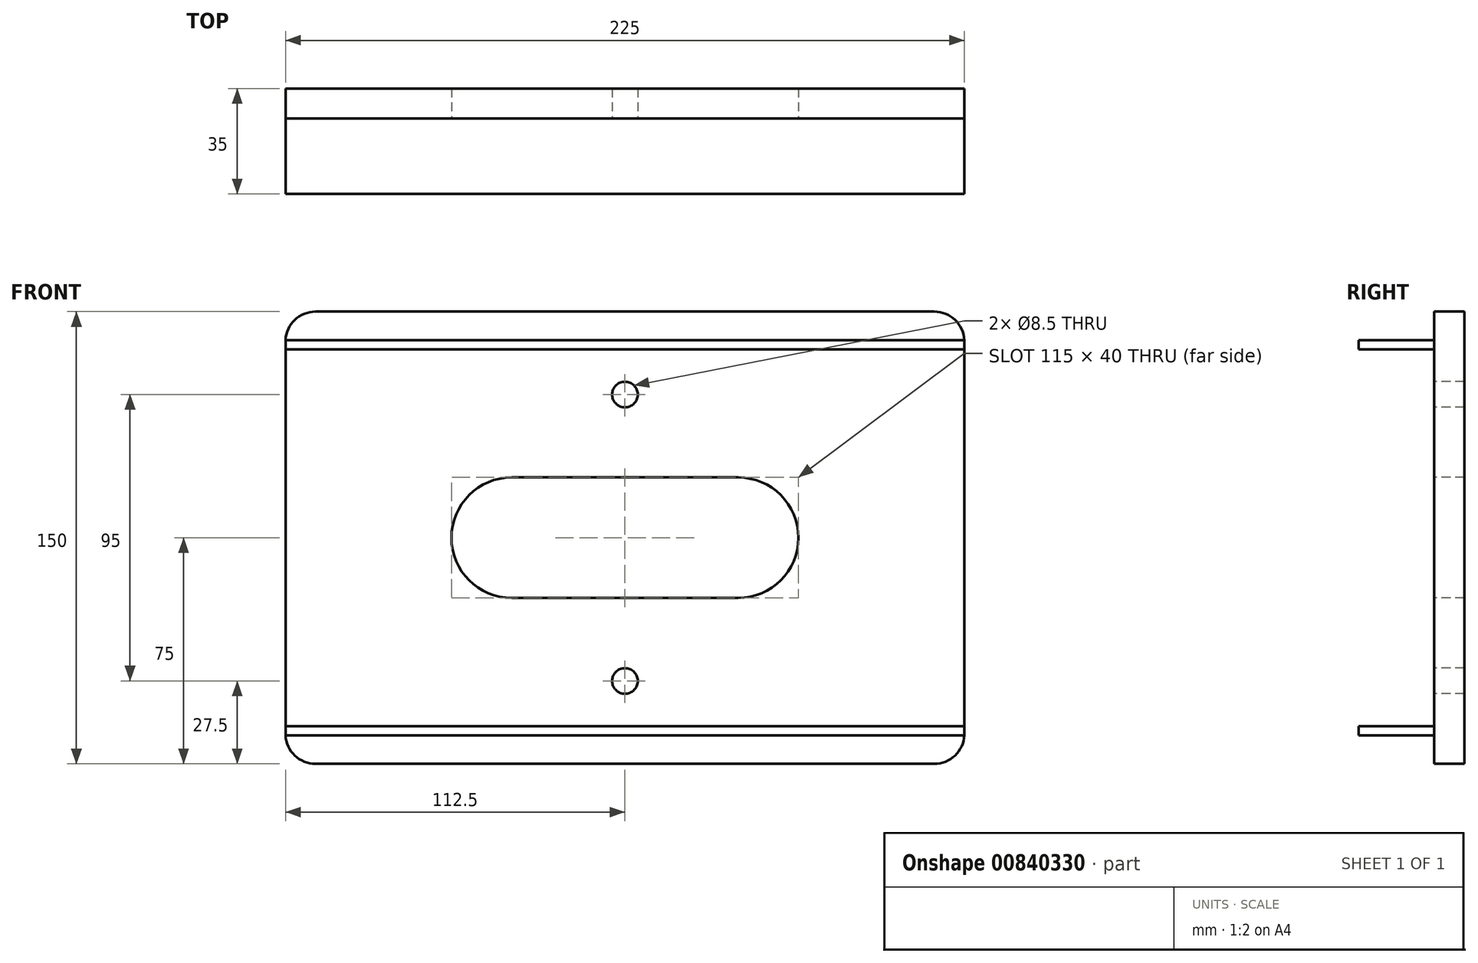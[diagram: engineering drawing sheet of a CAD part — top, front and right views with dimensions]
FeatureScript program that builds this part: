
annotation { "Feature Type Name" : "Feature", "Feature Type Description" : "" }
export const myFeature = defineFeature(function(context is Context, id is Id, definition is map)
    precondition{}
    {
        {
            var Q0;
            Q0=qCreatedBy(makeId("Front.planeOp"),FACE);
            var sketch = newSketch(context, id + "F0", { "sketchPlane" : qUnion([Q0])});
            skLineSegment(sketch, "E0.bottom", {"start": v(-112.5, 75) * mm, "end": v(112.5, 75) * mm});
            skLineSegment(sketch, "E0.top", {"start": v(-112.5, -75) * mm, "end": v(112.5, -75) * mm});
            skLineSegment(sketch, "E0.left", {"start": v(-112.5, 75) * mm, "end": v(-112.5, -75) * mm});
            skLineSegment(sketch, "E0.right", {"start": v(112.5, 75) * mm, "end": v(112.5, -75) * mm});
            skPoint(sketch, "E0.middle", {"position": v(0, 0) * mm});
            skCircle(sketch, "E1", {"center": v(0, 0) * mm, "radius": 20 * mm});
            skSolve(sketch);
        }
        {
            var Q0;
            Q0=qSketchRegion(id+"F0",true);
            extrude(context, id + "F1", {"entities" : qUnion([Q0]), "endBound" : BoundingType.SYMMETRIC, "depth" : 10 * mm, "offsetDistance" : 25 * mm});
        }
        {
            var Q0;
            Q0=makeQuery(id+"F1.opExtrude","SWEPT_EDGE",EDGE,{"disambiguationData":[OSD([sQuery(id+"F0.wireOp",EDGE,"E0.bottom"),sQuery(id+"F0.wireOp",EDGE,"E0.left")])]});
            var Q1;
            Q1=makeQuery(id+"F1.opExtrude","SWEPT_EDGE",EDGE,{"disambiguationData":[OSD([sQuery(id+"F0.wireOp",EDGE,"E0.bottom"),sQuery(id+"F0.wireOp",EDGE,"E0.right")])]});
            var Q2;
            Q2=makeQuery(id+"F1.opExtrude","SWEPT_EDGE",EDGE,{"disambiguationData":[OSD([sQuery(id+"F0.wireOp",EDGE,"E0.top"),sQuery(id+"F0.wireOp",EDGE,"E0.right")])]});
            var Q3;
            Q3=makeQuery(id+"F1.opExtrude","SWEPT_EDGE",EDGE,{"disambiguationData":[OSD([sQuery(id+"F0.wireOp",EDGE,"E0.top"),sQuery(id+"F0.wireOp",EDGE,"E0.left")])]});
            fillet(context, id + "F2", {"entities" : qUnion([Q0, Q1, Q2, Q3]), "radius" : 10 * mm, "tangentPropagation" : true, "allowEdgeOverflow" : false});
        }
        {
            var Q0;
            Q0=makeQuery(id+"F1.opExtrude","CAP_FACE",FACE,{"disambiguationData":[OSD([sQuery(id+"F0.wireOp",EDGE,"E0.bottom"),sQuery(id+"F0.wireOp",EDGE,"E0.top"),sQuery(id+"F0.wireOp",EDGE,"E0.left"),sQuery(id+"F0.wireOp",EDGE,"E0.right"),sQuery(id+"F0.wireOp",EDGE,"E1")])],"isStart":false});
            var sketch = newSketch(context, id + "F3", { "sketchPlane" : qUnion([Q0])});
            skLineSegment(sketch, "E2", {"start": v(-37.5, 0) * mm, "end": v(37.5, 0) * mm});
            skArc(sketch, "E3.0.startCap", {"start": v(-37.5, -20) * mm, "mid": v(-57.5, 0) * mm, "end": v(-37.5, 20) * mm});
            skArc(sketch, "E3.0.endCap", {"start": v(37.5, 20) * mm, "mid": v(57.5, 0) * mm, "end": v(37.5, -20) * mm});
            skLineSegment(sketch, "E3.0.left", {"start": v(-37.5, 20) * mm, "end": v(37.5, 20) * mm});
            skLineSegment(sketch, "E3.0.right", {"start": v(-37.5, -20) * mm, "end": v(37.5, -20) * mm});
            skSolve(sketch);
        }
        {
            var Q0;
            Q0=qSketchRegion(id+"F3",true);
            extrude(context, id + "F4", {"entities" : qUnion([Q0]), "operationType" : NewBodyOperationType.REMOVE, "endBound" : BoundingType.THROUGH_ALL, "oppositeDirection" : true, "depth" : 25 * mm, "offsetDistance" : 25 * mm});
        }
        {
            var Q0;
            Q0=makeQuery(id+"F1.opExtrude","CAP_FACE",FACE,{"disambiguationData":[OSD([sQuery(id+"F0.wireOp",EDGE,"E0.bottom"),sQuery(id+"F0.wireOp",EDGE,"E0.top"),sQuery(id+"F0.wireOp",EDGE,"E0.left"),sQuery(id+"F0.wireOp",EDGE,"E0.right"),sQuery(id+"F0.wireOp",EDGE,"E1")])],"isStart":false});
            var sketch = newSketch(context, id + "F5", { "sketchPlane" : qUnion([Q0])});
            skLineSegment(sketch, "E4.bottom", {"start": v(-112.5, 62.5) * mm, "end": v(112.5, 62.5) * mm});
            skLineSegment(sketch, "E4.top", {"start": v(-112.5, 65.5) * mm, "end": v(112.5, 65.5) * mm});
            skLineSegment(sketch, "E4.left", {"start": v(-112.5, 62.5) * mm, "end": v(-112.5, 65.5) * mm});
            skLineSegment(sketch, "E4.right", {"start": v(112.5, 62.5) * mm, "end": v(112.5, 65.5) * mm});
            skLineSegment(sketch, "E5.bottom", {"start": v(-112.5, -65.5) * mm, "end": v(112.5, -65.5) * mm});
            skLineSegment(sketch, "E5.top", {"start": v(-112.5, -62.5) * mm, "end": v(112.5, -62.5) * mm});
            skLineSegment(sketch, "E5.left", {"start": v(-112.5, -65.5) * mm, "end": v(-112.5, -62.5) * mm});
            skLineSegment(sketch, "E5.right", {"start": v(112.5, -65.5) * mm, "end": v(112.5, -62.5) * mm});
            skSolve(sketch);
        }
        {
            var Q0;
            Q0 = qSketchRegion(id + "F5", true);
            extrude(context, id + "F6", {"entities" : qUnion([Q0]), "depth" : 25 * mm, "offsetDistance" : 25 * mm});
        }
        {
            var Q0;
            Q0=makeQuery(id+"F1.opExtrude","CAP_FACE",FACE,{"disambiguationData":[OSD([sQuery(id+"F0.wireOp",EDGE,"E0.bottom"),sQuery(id+"F0.wireOp",EDGE,"E0.top"),sQuery(id+"F0.wireOp",EDGE,"E0.left"),sQuery(id+"F0.wireOp",EDGE,"E0.right"),sQuery(id+"F0.wireOp",EDGE,"E1")])],"isStart":false});
            var sketch = newSketch(context, id + "F7", { "sketchPlane" : qUnion([Q0])});
            skPoint(sketch, "E6", {"position": v(0, 47.5) * mm});
            skPoint(sketch, "E7", {"position": v(0, -47.5) * mm});
            skSolve(sketch);
        }
        {
            var Q0;
            Q0=sQuery(id+"F7.wireOp",VERTEX,"E6");
            var Q1;
            Q1=sQuery(id+"F7.wireOp",VERTEX,"E7");
            var Q2;
            Q2=makeQuery(id+"F1.opExtrude","SWEPT_BODY",BODY,{"disambiguationData":[OSD([sQuery(id+"F0.wireOp",EDGE,"E0.bottom"),sQuery(id+"F0.wireOp",EDGE,"E0.top"),sQuery(id+"F0.wireOp",EDGE,"E0.left"),sQuery(id+"F0.wireOp",EDGE,"E0.right"),sQuery(id+"F0.wireOp",EDGE,"E1")])]});
            hole(context, id + "F8", {"style" : HoleStyle.SIMPLE, "endStyle" : HoleEndStyle.BLIND, "standardTappedOrClearance" : lookupTablePath({ "standard" : "ISO", "engagement" : "75%", "pitch" : "1.5 mm", "size" : "M10", "type" : "Tapped" }), "standardBlindInLast" : lookupTablePath({ "standard" : "ISO", "engagement" : "75%", "pitch" : "1.5 mm", "size" : "M10", "type" : "Tapped" }), "holeDiameter" : 8.5 * mm, "majorDiameter" : 10 * mm, "showTappedDepth" : true, "holeDepth" : 24.5 * mm, "isTappedThrough" : true, "tappedDepth" : 20 * mm, "tapClearance" : 3, "startFromSketch" : true, "locations" : qUnion([Q0, Q1]), "scope" : qUnion([Q2])});
        }
    });
